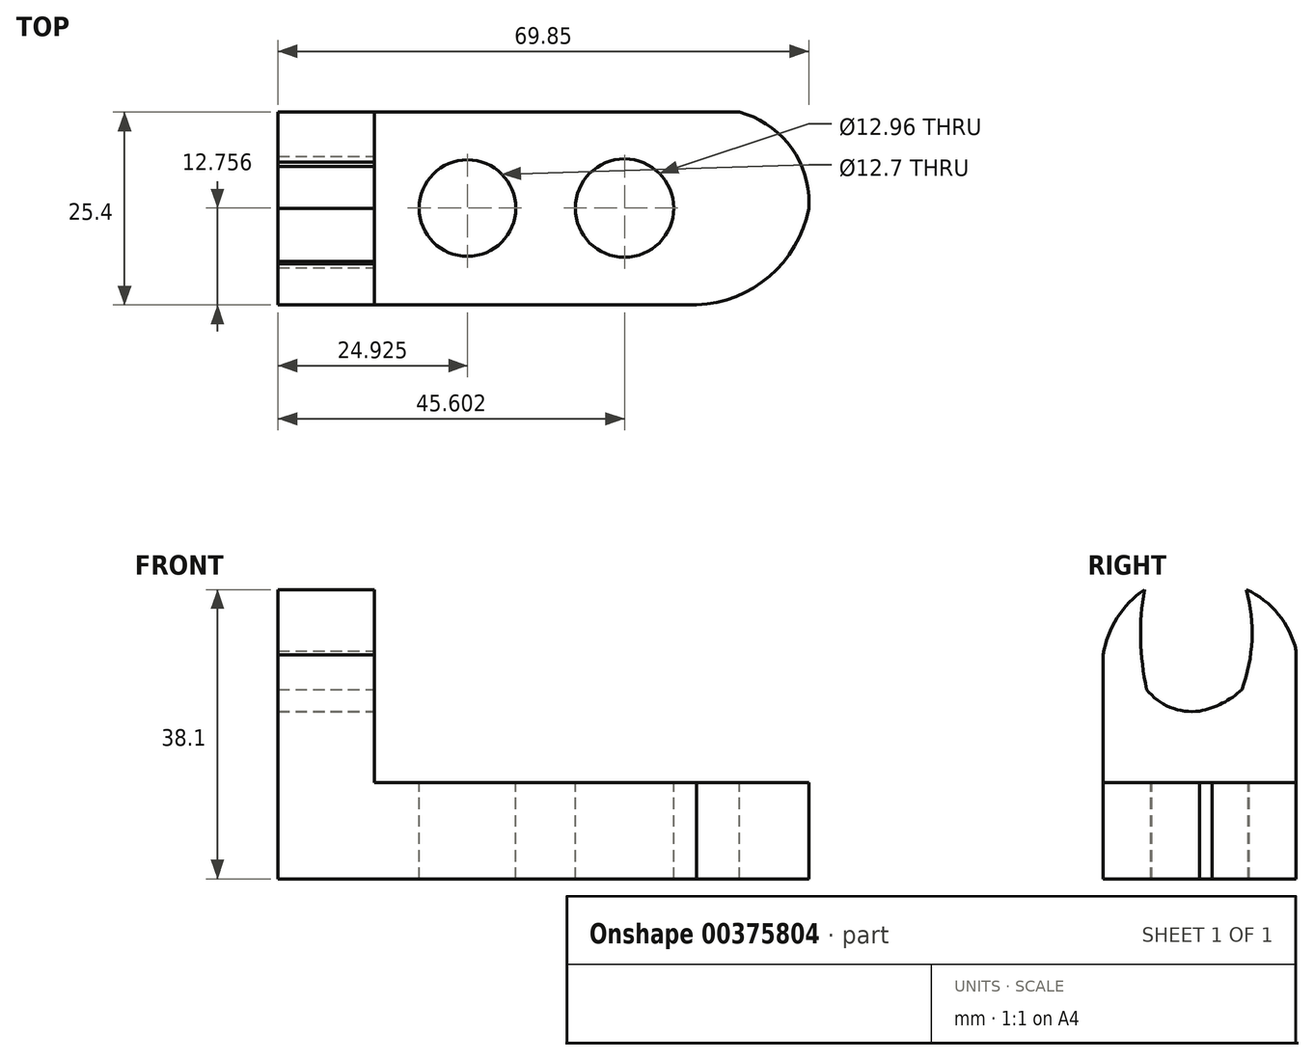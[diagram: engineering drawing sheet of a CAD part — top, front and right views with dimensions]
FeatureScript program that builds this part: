
annotation { "Feature Type Name" : "Feature", "Feature Type Description" : "" }
export const myFeature = defineFeature(function(context is Context, id is Id, definition is map)
    precondition{}
    {
        {
            var Q0;
            Q0=qCreatedBy(makeId("Front.planeOp"),FACE);
            var sketch = newSketch(context, id + "F0", { "sketchPlane" : qUnion([Q0])});
            skLineSegment(sketch, "E0", {"start": v(0, 0) * mm, "end": v(69.85, 0) * mm});
            skLineSegment(sketch, "E1", {"start": v(69.85, 0) * mm, "end": v(69.85, 12.7) * mm});
            skLineSegment(sketch, "E2", {"start": v(69.85, 12.7) * mm, "end": v(12.7, 12.7) * mm});
            skLineSegment(sketch, "E3", {"start": v(12.7, 12.7) * mm, "end": v(12.7, 38.1) * mm});
            skLineSegment(sketch, "E4", {"start": v(12.7, 38.1) * mm, "end": v(0, 38.1) * mm});
            skLineSegment(sketch, "E5", {"start": v(0, 38.1) * mm, "end": v(0, 0) * mm});
            skSolve(sketch);
        }
        {
            var Q0;
            Q0 = qSketchRegion(id + "F0", true);
            extrude(context, id + "F1", {"entities" : qUnion([Q0]), "depth" : 25.4 * mm});
        }
        {
            var Q0;
            Q0=makeQuery(id+"F1.opExtrude","SWEPT_FACE",FACE,{"disambiguationData":[OSD([sQuery(id+"F0.wireOp",EDGE,"E2")])]});
            var sketch = newSketch(context, id + "F2", { "sketchPlane" : qUnion([Q0])});
            skArc(sketch, "E6", {"start": v(53.86, -25.4) * mm, "mid": v(64.21, -22.02) * mm, "end": v(69.85, -12.7) * mm});
            skArc(sketch, "E7", {"start": v(69.85, -12.7) * mm, "mid": v(65.42, -2.41) * mm, "end": v(54.48, 0) * mm});
            skSolve(sketch);
        }
        {
            var Q0;
            {var subQ0=sQuery(id+"F2.wireOp",EDGE,"E6");var subQ1=sQuery(id+"F0.wireOp",EDGE,"E2");var subQ4=makeQuery(id+"F1.opExtrude","CAP_EDGE",EDGE,{"disambiguationData":[OSD([subQ1])],"isStart":false});var subQ5=makeQuery(id+"F2.imprint","INTERSECT",VERTEX,{"disambiguationData":[OD(1.0)],"derivedFrom":[subQ4,subQ0]});Q0=makeQuery(id+"F2.imprint","IMPRINT",FACE,{"disambiguationData":[TD([[makeQuery(id+"F2.imprint","IMPRINT",EDGE,{"disambiguationData":[TD([[subQ5,1.0]])],"derivedFrom":subQ4}),-1.0]])]});}
            var Q1;
            {var subQ0=sQuery(id+"F2.wireOp",EDGE,"E7");var subQ1=sQuery(id+"F0.wireOp",EDGE,"E2");var subQ4=makeQuery(id+"F1.opExtrude","CAP_EDGE",EDGE,{"disambiguationData":[OSD([subQ1])],"isStart":true});var subQ5=makeQuery(id+"F2.imprint","INTERSECT",VERTEX,{"disambiguationData":[OD(1.0)],"derivedFrom":[subQ4,subQ0]});Q1=makeQuery(id+"F2.imprint","IMPRINT",FACE,{"disambiguationData":[TD([[makeQuery(id+"F2.imprint","IMPRINT",EDGE,{"disambiguationData":[TD([[subQ5,1.0]])],"derivedFrom":subQ0}),-1.0]])]});}
            extrude(context, id + "F3", {"entities" : qUnion([Q0, Q1]), "operationType" : NewBodyOperationType.REMOVE, "oppositeDirection" : true, "depth" : 25.4 * mm});
        }
        {
            var Q0;
            Q0=makeQuery(id+"F1.opExtrude","SWEPT_FACE",FACE,{"disambiguationData":[OSD([sQuery(id+"F0.wireOp",EDGE,"E3")])]});
            var sketch = newSketch(context, id + "F4", { "sketchPlane" : qUnion([Q0])});
            skArc(sketch, "E8", {"start": v(-7.13, 24.96) * mm, "mid": v(-5.81, 31.48) * mm, "end": v(-6.56, 38.1) * mm});
            skArc(sketch, "E9", {"start": v(-12.7, 22.1) * mm, "mid": v(-9.71, 23.14) * mm, "end": v(-7.13, 24.96) * mm});
            skPoint(sketch, "E9.startSnap0", {"position": v(-12.7, 38.1) * mm});
            skArc(sketch, "E10", {"start": v(-19.97, 38.1) * mm, "mid": v(-20.47, 31.52) * mm, "end": v(-19.68, 24.96) * mm});
            skArc(sketch, "E11", {"start": v(-19.68, 24.96) * mm, "mid": v(-16.57, 22.6) * mm, "end": v(-12.7, 22.1) * mm});
            skSolve(sketch);
        }
        {
            var Q0;
            Q0 = qSketchRegion(id + "F4", true);
            var Q1;
            {var subQ1=sQuery(id+"F4.wireOp",EDGE,"E8");Q1=makeQuery(id+"F4.imprint","IMPRINT",FACE,{"disambiguationData":[TD([[makeQuery(id+"F4.imprint","IMPRINT",EDGE,{"derivedFrom":subQ1}),1.0]])]});}
            extrude(context, id + "F5", {"entities" : qUnion([Q0, Q1]), "operationType" : NewBodyOperationType.REMOVE, "oppositeDirection" : true, "depth" : 25.4 * mm});
        }
        {
            var Q0;
            Q0=makeQuery(id+"F1.opExtrude","SWEPT_FACE",FACE,{"disambiguationData":[OSD([sQuery(id+"F0.wireOp",EDGE,"E3")])]});
            var sketch = newSketch(context, id + "F6", { "sketchPlane" : qUnion([Q0])});
            skArc(sketch, "E12", {"start": v(-19.97, 38.1) * mm, "mid": v(-24.53, 32.54) * mm, "end": v(-25.4, 25.4) * mm});
            skArc(sketch, "E13", {"start": v(0, 24.96) * mm, "mid": v(-0.94, 32.7) * mm, "end": v(-6.56, 38.1) * mm});
            skSolve(sketch);
        }
        {
            var Q0;
            Q0 = qSketchRegion(id + "F6", true);
            var Q1;
            {var subQ1=sQuery(id+"F0.wireOp",EDGE,"E4");var subQ2=sQuery(id+"F0.wireOp",EDGE,"E3");var subQ3=sQuery(id+"F4.wireOp",EDGE,"E10");var subQ4=makeQuery(id+"F5.boolean.opBoolean","SPLIT",EDGE,{"disambiguationData":[TD([makeQuery(id+"F5.opExtrude","SWEPT_FACE",FACE,{"disambiguationData":[OSD([subQ3])]})])],"derivedFrom":makeQuery(id+"F1.opExtrude","SWEPT_EDGE",EDGE,{"disambiguationData":[OSD([subQ2,subQ1])]})});Q1=makeQuery(id+"F6.imprint","IMPRINT",FACE,{"disambiguationData":[TD([[makeQuery(id+"F6.imprint","IMPRINT",EDGE,{"derivedFrom":subQ4}),-1.0]])]});}
            var Q2;
            {var subQ1=sQuery(id+"F0.wireOp",EDGE,"E4");var subQ2=sQuery(id+"F0.wireOp",EDGE,"E3");var subQ3=sQuery(id+"F4.wireOp",EDGE,"E8");var subQ4=makeQuery(id+"F5.boolean.opBoolean","SPLIT",EDGE,{"disambiguationData":[TD([makeQuery(id+"F5.opExtrude","SWEPT_FACE",FACE,{"disambiguationData":[OSD([subQ3])]})])],"derivedFrom":makeQuery(id+"F1.opExtrude","SWEPT_EDGE",EDGE,{"disambiguationData":[OSD([subQ2,subQ1])]})});Q2=makeQuery(id+"F6.imprint","IMPRINT",FACE,{"disambiguationData":[TD([[makeQuery(id+"F6.imprint","IMPRINT",EDGE,{"derivedFrom":subQ4}),-1.0]])]});}
            extrude(context, id + "F7", {"entities" : qUnion([Q0, Q1, Q2]), "operationType" : NewBodyOperationType.REMOVE, "oppositeDirection" : true, "depth" : 25.4 * mm});
        }
        {
            var Q0;
            {var subQ0=sQuery(id+"F0.wireOp",EDGE,"E2");var subQ1=makeQuery(id+"F1.opExtrude","SWEPT_EDGE",EDGE,{"disambiguationData":[OSD([subQ0,sQuery(id+"F0.wireOp",EDGE,"E3")])]});Q0=makeQuery(id+"F2.imprint","IMPRINT",FACE,{"disambiguationData":[TD([[makeQuery(id+"F2.imprint","IMPRINT",EDGE,{"derivedFrom":subQ1}),-1.0]])]});}
            var sketch = newSketch(context, id + "F8", { "sketchPlane" : qUnion([Q0])});
            skCircle(sketch, "E14", {"center": v(24.92, -12.64) * mm, "radius": 6.35 * mm});
            skCircle(sketch, "E15", {"center": v(45.6, -12.64) * mm, "radius": 6.48 * mm});
            skSolve(sketch);
        }
        {
            var Q0;
            Q0 = qSketchRegion(id + "F8", true);
            extrude(context, id + "F9", {"entities" : qUnion([Q0]), "operationType" : NewBodyOperationType.REMOVE, "oppositeDirection" : true, "depth" : 25.4 * mm});
        }
    });
